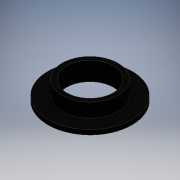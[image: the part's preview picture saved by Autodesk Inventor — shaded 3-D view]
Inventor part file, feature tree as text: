
AUTODESK INVENTOR PART (.ipt)
format: ipt  version: 2016 (Build 200138000, 138)  size: 103,936 bytes
history: native  units: mm
features: extrude x2, other x1, sketch x1
ambient origin geometry x8: Origin, YZ Plane, XZ Plane, XY Plane, X Axis, Y Axis, Z Axis, Center Point
bodies: Body1 (feature_tree)
feature tree (4):
  other  "ソリッド1"
  sketch  "スケッチ1"
  extrude  "押し出し1"  Depth=10.0mm
  extrude  "押し出し2"  Depth=12.0mm
